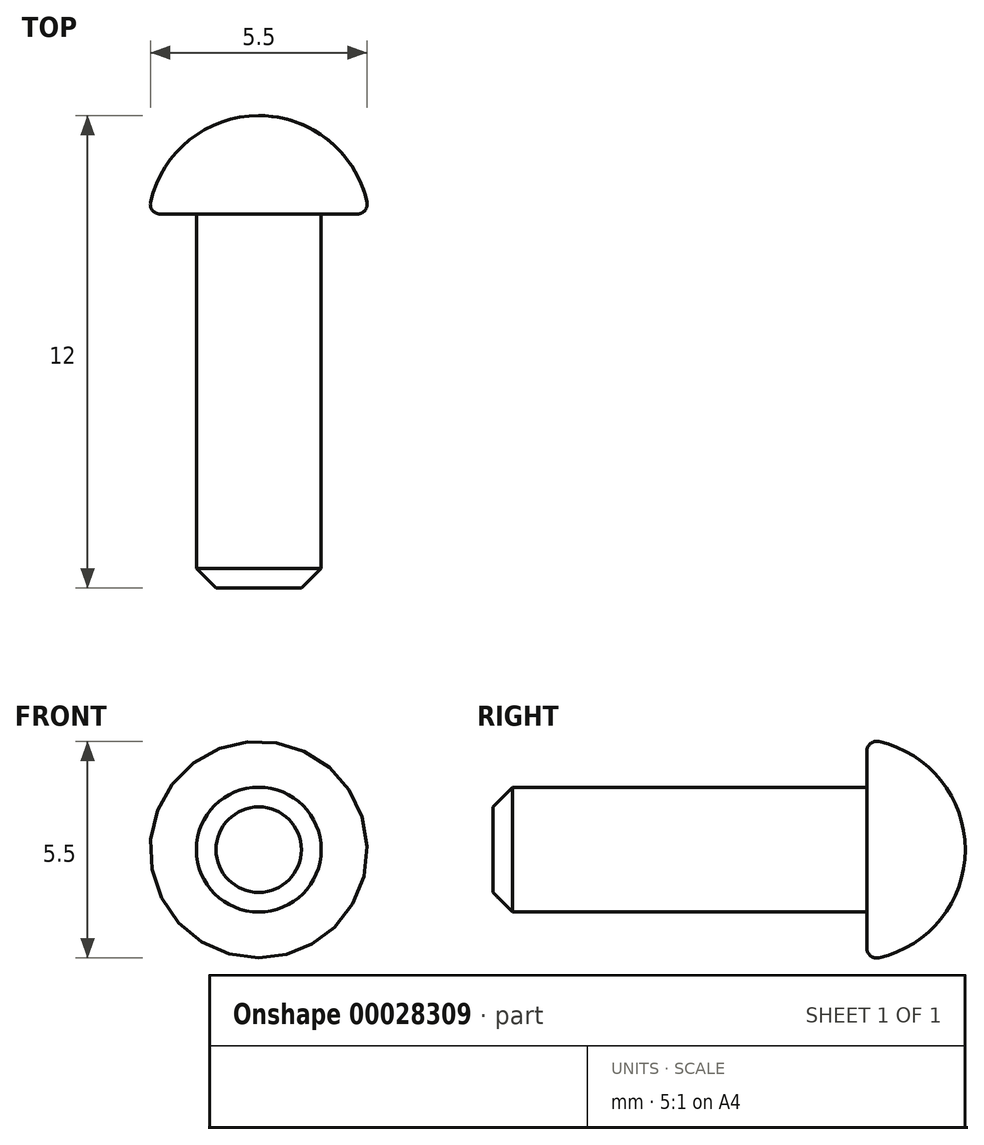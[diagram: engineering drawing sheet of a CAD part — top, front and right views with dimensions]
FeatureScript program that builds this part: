
annotation { "Feature Type Name" : "Feature", "Feature Type Description" : "" }
export const myFeature = defineFeature(function(context is Context, id is Id, definition is map)
    precondition{}
    {
        {
            var Q0;
            Q0=qCreatedBy(makeId("Top.planeOp"),FACE);
            var sketch = newSketch(context, id + "F0", { "sketchPlane" : qUnion([Q0])});
            skLineSegment(sketch, "E0", {"start": v(0, 0) * mm, "end": v(0, 12) * mm, "construction": true});
            skLineSegment(sketch, "E1", {"start": v(0, 0) * mm, "end": v(1.58, 0) * mm});
            skLineSegment(sketch, "E2", {"start": v(1.58, 0) * mm, "end": v(1.58, 9.5) * mm});
            skLineSegment(sketch, "E3", {"start": v(1.58, 9.5) * mm, "end": v(2.8, 9.5) * mm});
            skLineSegment(sketch, "E4.MirrorCS", {"start": v(-1.58, 9.5) * mm, "end": v(-2.8, 9.5) * mm});
            skLineSegment(sketch, "E5.MirrorCS", {"start": v(-1.58, 0) * mm, "end": v(-1.58, 9.5) * mm});
            skLineSegment(sketch, "E6.MirrorCS", {"start": v(0, 0) * mm, "end": v(-1.58, 0) * mm});
            skArc(sketch, "E7", {"start": v(2.8, 9.5) * mm, "mid": v(0, 12) * mm, "end": v(-2.8, 9.5) * mm});
            skLineSegment(sketch, "E8", {"start": v(0, 0) * mm, "end": v(0, 12) * mm});
            skSolve(sketch);
        }
        {
            var Q0;
            Q0=makeQuery(id+"F0.imprint","IMPRINT",FACE,{"disambiguationData":[TD([[makeQuery(id+"F0.imprint","IMPRINT",EDGE,{"derivedFrom":sQuery(id+"F0.wireOp",EDGE,"E1")}),1.0]])]});
            var Q1;
            Q1=sQuery(id+"F0.wireOp",EDGE,"E8");
            revolve(context, id + "F1", {"entities" : qUnion([Q0]), "axis" : qUnion([Q1]), "revolveType" : RevolveType.FULL});
        }
        {
            var Q0;
            Q0=makeQuery(id+"F1.opRevolve","SWEPT_EDGE",EDGE,{"disambiguationData":[OSD([sQuery(id+"F0.wireOp",EDGE,"E1"),sQuery(id+"F0.wireOp",EDGE,"E2")])]});
            chamfer(context, id + "F2", {"entities" : qUnion([Q0]), "width" : 0.5 * mm, "tangentPropagation" : true});
        }
        {
            var Q0;
            Q0=makeQuery(id+"F1.opRevolve","SWEPT_EDGE",EDGE,{"disambiguationData":[OSD([sQuery(id+"F0.wireOp",EDGE,"E3"),sQuery(id+"F0.wireOp",EDGE,"E7")])]});
            fillet(context, id + "F3", {"entities" : qUnion([Q0]), "radius" : 0.25 * mm, "tangentPropagation" : true, "allowEdgeOverflow" : false});
        }
    });
